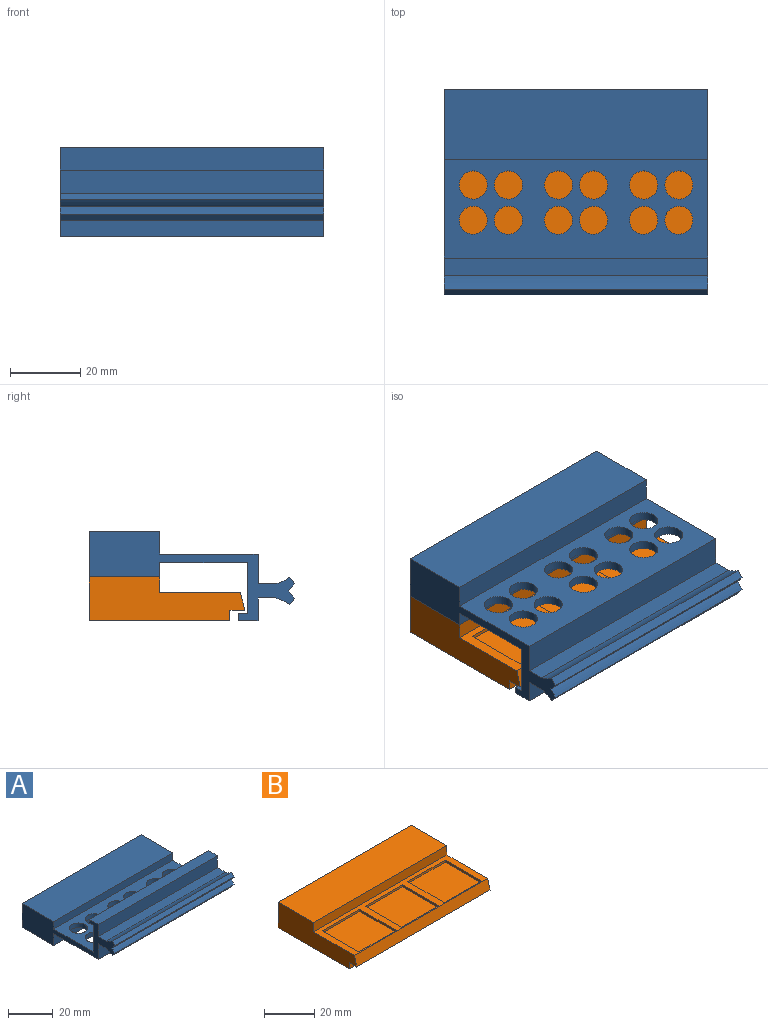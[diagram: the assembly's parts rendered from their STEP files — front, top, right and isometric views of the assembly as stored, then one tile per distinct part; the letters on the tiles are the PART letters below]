
ASSEMBLY  parts=2 mates=1
PART A: 39 faces, bbox 75x58.5x25.5 mm
  f0: plane 3x3mm, normal (0,1,0), area 7.1mm2, adj f14
  f1: plane 3x3mm, normal (0,1,0), area 7.1mm2, adj f15
  f2: cylinder r=4mm len=8mm, axis (0,0,-1), area 62.8mm2, adj f16,f27
  f3: cylinder r=4mm len=8mm, axis (0,0,-1), area 62.8mm2, adj f16,f27
  f4: cylinder r=4mm len=8mm, axis (0,0,-1), area 62.8mm2, adj f16,f27
  f5: cylinder r=4mm len=8mm, axis (0,0,-1), area 62.8mm2, adj f16,f27
  f6: cylinder r=4mm len=8mm, axis (0,0,-1), area 62.8mm2, adj f16,f27
  f7: cylinder r=4mm len=8mm, axis (0,0,-1), area 62.8mm2, adj f16,f27
  f8: cylinder r=4mm len=8mm, axis (0,0,-1), area 62.8mm2, adj f16,f27
  f9: cylinder r=4mm len=8mm, axis (0,0,-1), area 62.8mm2, adj f16,f27
  f10: cylinder r=4mm len=8mm, axis (0,0,-1), area 62.8mm2, adj f16,f27
  f11: cylinder r=4mm len=8mm, axis (0,0,-1), area 62.8mm2, adj f16,f27
  f12: cylinder r=4mm len=8mm, axis (0,0,-1), area 62.8mm2, adj f16,f27
  f13: cylinder r=4mm len=8mm, axis (0,0,-1), area 62.8mm2, adj f16,f27
  f14: cylinder r=1.5mm len=10.5mm, axis (0,-1,0), area 99mm2, adj f0,f30
  f15: cylinder r=1.5mm len=10.5mm, axis (0,-1,0), area 99mm2, adj f1,f30
  f16: plane 75x25mm, normal (0,0,1), area 1271.8mm2, adj f2,f3,f4,f5,f6,f7,f8,f9
  f17: plane 75x14.5mm, normal (0,1,0), area 1087.5mm2, adj f16,f18,f34,f36
  f18: plane 75x2.6mm, normal (0,0,-1), area 195mm2, adj f17,f33,f34,f36
  f19: cylinder r=10.11mm len=75mm, axis (-1,0,0), area 330.2mm2, adj f20,f34,f35,f36
  f20: plane 75x1.81mm, normal (0,-0.76,0.65), area 177.9mm2, adj f19,f21,f34,f36
  f21: cylinder r=10.05mm len=75mm, axis (-1,0,0), area 210.9mm2, adj f20,f22,f34,f36
  f22: cylinder r=10.05mm len=75mm, axis (-1,0,0), area 210.9mm2, adj f21,f23,f34,f36
  f23: plane 75x1.81mm, normal (0,-0.76,-0.65), area 177.9mm2, adj f22,f24,f34,f36
  f24: cylinder r=10.11mm len=75mm, axis (-1,0,0), area 330.3mm2, adj f23,f25,f34,f36
  f25: plane 75x5mm, normal (0,0,-1), area 375mm2, adj f24,f26,f34,f36
  f26: plane 75x8.5mm, normal (0,-1,0), area 637.5mm2, adj f25,f27,f34,f36
  f27: plane 75x28mm, normal (0,0,-1), area 1496.8mm2, adj f2,f3,f4,f5,f6,f7,f8,f9
  f28: plane 75x6.5mm, normal (0,-1,0), area 487.5mm2, adj f27,f29,f34,f36
  f29: plane 75x20mm, normal (0,0,-1), area 1500mm2, adj f28,f30,f34,f36
  f30: plane 75x13mm, normal (0,1,0), area 960.9mm2, adj f14,f15,f29,f31,f34,f36
  f31: plane 75x20mm, normal (0,0,1), area 1500mm2, adj f30,f32,f34,f36
  f32: plane 75x4mm, normal (0,-1,0), area 300mm2, adj f16,f31,f34,f36
  f33: plane 75x2mm, normal (0,1,0), area 150mm2, adj f18,f34,f36,f37
  f34: plane 58.46x25.5mm, normal (-1,0,0), area 432.3mm2, adj f16,f17,f18,f19,f20,f21,f22,f23
  f35: plane 75x5mm, normal (0,0,1), area 375mm2, adj f19,f34,f36,f38
  f36: plane 58.46x25.5mm, normal (1,0,0), area 432.3mm2, adj f16,f17,f18,f19,f20,f21,f22,f23
  f37: plane 75x5.6mm, normal (0,0,1), area 420mm2, adj f33,f34,f36,f38
  f38: plane 75x6.5mm, normal (0,-1,0), area 487.5mm2, adj f34,f35,f36,f37
PART B: 29 faces, bbox 75x44.3x12.5 mm
  f0: plane 3x3mm, normal (0,1,0), area 7.1mm2, adj f2
  f1: plane 3x3mm, normal (0,1,0), area 7.1mm2, adj f3
  f2: cylinder r=1.5mm len=10mm, axis (0,-1,0), area 94.2mm2, adj f0,f4
  f3: cylinder r=1.5mm len=10mm, axis (0,-1,0), area 94.2mm2, adj f1,f4
  f4: plane 75x12.5mm, normal (0,1,0), area 923.4mm2, adj f2,f3,f5,f8,f13,f15
  f5: plane 75x20mm, normal (0,0,1), area 1500mm2, adj f4,f12,f13,f15
  f6: plane 75x4.25mm, normal (0,0,-1), area 318.8mm2, adj f7,f13,f14,f15
  f7: plane 75x3mm, normal (0,-1,0), area 225mm2, adj f6,f8,f13,f15
  f8: plane 75x40mm, normal (0,0,-1), area 3000mm2, adj f4,f7,f13,f15
  f9: plane 21x20.5mm, normal (0,0,1), area 430.5mm2, adj f16,f17,f18,f19
  f10: plane 21x20.5mm, normal (0,0,1), area 430.5mm2, adj f20,f21,f22,f23
  f11: plane 21x20.5mm, normal (0,0,1), area 430.5mm2, adj f24,f25,f26,f27
  f12: plane 75x4.5mm, normal (0,-1,0), area 337.5mm2, adj f5,f13,f15,f28
  f13: plane 44.25x12.5mm, normal (-1,0,0), area 428.1mm2, adj f4,f5,f6,f7,f8,f12,f14,f28
  f14: plane 75x5mm, normal (0,-0.97,0.24), area 386.5mm2, adj f6,f13,f15,f28
  f15: plane 44.25x12.5mm, normal (1,0,0), area 428.1mm2, adj f4,f5,f6,f7,f8,f12,f14,f28
  f16: plane 20.5x1mm, normal (-1,0,0), area 20.5mm2, adj f9,f17,f19,f28
  f17: plane 21x1mm, normal (0,1,0), area 21mm2, adj f9,f16,f18,f28
  f18: plane 20.5x1mm, normal (1,0,0), area 20.5mm2, adj f9,f17,f19,f28
  f19: plane 21x1mm, normal (0,-1,0), area 21mm2, adj f9,f16,f18,f28
  f20: plane 20.5x1mm, normal (-1,0,0), area 20.5mm2, adj f10,f21,f23,f28
  f21: plane 21x1mm, normal (0,1,0), area 21mm2, adj f10,f20,f22,f28
  f22: plane 20.5x1mm, normal (1,0,0), area 20.5mm2, adj f10,f21,f23,f28
  f23: plane 21x1mm, normal (0,-1,0), area 21mm2, adj f10,f20,f22,f28
  f24: plane 20.5x1mm, normal (-1,0,0), area 20.5mm2, adj f11,f25,f27,f28
  f25: plane 21x1mm, normal (0,1,0), area 21mm2, adj f11,f24,f26,f28
  f26: plane 20.5x1mm, normal (1,0,0), area 20.5mm2, adj f11,f25,f27,f28
  f27: plane 21x1mm, normal (0,-1,0), area 21mm2, adj f11,f24,f26,f28
  f28: plane 75x23mm, normal (0,0,1), area 433.5mm2, adj f12,f13,f14,f15,f16,f17,f18,f19
PLACE A rot(axis=(0,1,0),180deg) t=(-13.84,-12.24,23.44)mm
PLACE B t=(-13.84,-12.24,2.94)mm
MATE fastened A.f31 <-> B.f5  axis (0,0,-1) through (-13.84,10.26,15.44)mm
